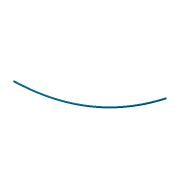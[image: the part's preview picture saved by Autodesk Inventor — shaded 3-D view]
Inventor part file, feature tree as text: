
AUTODESK INVENTOR PART (.ipt)
format: ipt  version: 2016 (Build 200138000, 138)  size: 371,200 bytes
history: native  units: in
note: dims shown in document units (in); Inventor stores cm internally (conversion verified against a paired STEP export)
features: sketch x14, extrude x5, other x5, hole x5, sweep x2, plane x1
ambient origin geometry x8: Origin, YZ Plane, XZ Plane, XY Plane, X Axis, Y Axis, Z Axis, Center Point
bodies: Solid1 (feature_tree)
feature tree (32):
  sweep  "fullLength"
  sweep  "removeSleeveSection"
  extrude  "insertion"  TaperAngle=0.0deg  [1 undecoded]
  other  "outerEnd"
  other  "outerAngle"
  extrude  "endScrew"  Depth=12.5374in TaperAngle=0.0deg
  other  "central"
  extrude  "alignmentTab"  Depth=4.7244in
  plane  "Work Plane8"
  hole  "vertSupport"  [1 undecoded]
  extrude  "overlapSupports"  Depth=0.1in
  hole  "overlap1_pvc"  [1 undecoded]
  hole  "overlap2"  [1 undecoded]
  hole  "overlap3"  [1 undecoded]
  hole  "overlap4"  [1 undecoded]
  extrude  "Extrusion24"  Depth=0.3937in
  sketch  "Sketch1"  dims[d0=0.0in d1=275.5906in d2=0.0in]
  other  "2D Equation Curve1"
  sketch  "Sketch2"  dims[d6=2.4803in d8=0.122in]
  sketch  "Sketch8"  dims[d16=0.0in d17=21.5374in d18=0.0in]
  other  "2D Equation Curve4"
  sketch  "Sketch9"  dims[d21=0.122in d50=12.5374in d51=0.0in]
  sketch  "Sketch16"  dims[d65=0.5in d66=4.7244in]
  sketch  "Sketch21"  dims[d67=6.0in d68=0.0in d94=1.0in d104=2.4803in]
  sketch  "Sketch33"  dims[d105=1.0in d106=0.1in]
  sketch  "Sketch40"  dims[d107=0.05in d108=0.0in d109=0.05in d110=0.0in]
  sketch  "Sketch42"  dims[d127=2.4803in d128=1.2402in]
  sketch  "Sketch43"  dims[d134=0.3937in]
  sketch  "Sketch44"  dims[d135=0.0394in d136=29.5276in d137=14.7638in d138=9.8425in d139=90.0deg d140=39.3701in d141=0.8108in d147=0.3937in]
  sketch  "Sketch45"  dims[d148=0.0394in d149=0.3937in]
  sketch  "Sketch46"  dims[d150=0.3937in d151=0.3937in]
  sketch  "Sketch47"  dims[d152=0.3937in d153=0.3937in d154=0.3937in d155=0.3937in d156=0.3937in d157=2.4803in d158=0.0in d159=0.0394in d160=0.0394in d161=29.5276in d162=14.7638in d163=9.8425in d164=90.0deg d165=39.3701in d166=0.8108in d167=0.0787in d168=0.0394in d169=29.5276in d170=14.7638in d171=9.8425in d172=90.0deg d173=1.2402in d174=0.8108in d175=0.0787in d176=0.0394in d177=29.5276in d178=14.7638in d179=9.8425in d180=90.0deg d181=1.2402in d182=0.8108in d183=0.0787in d184=0.0394in d185=29.5276in d186=14.7638in d187=9.8425in d188=90.0deg d189=1.2402in d190=0.8108in d191=0.0197in d192=0.0in d193=0.0in d194=0.0in]
note: 6 required parameter values undecoded (feature->parameter linkage not recoverable at this tier; creation-order binding heuristic only, values carry confidence <= 0.55)
